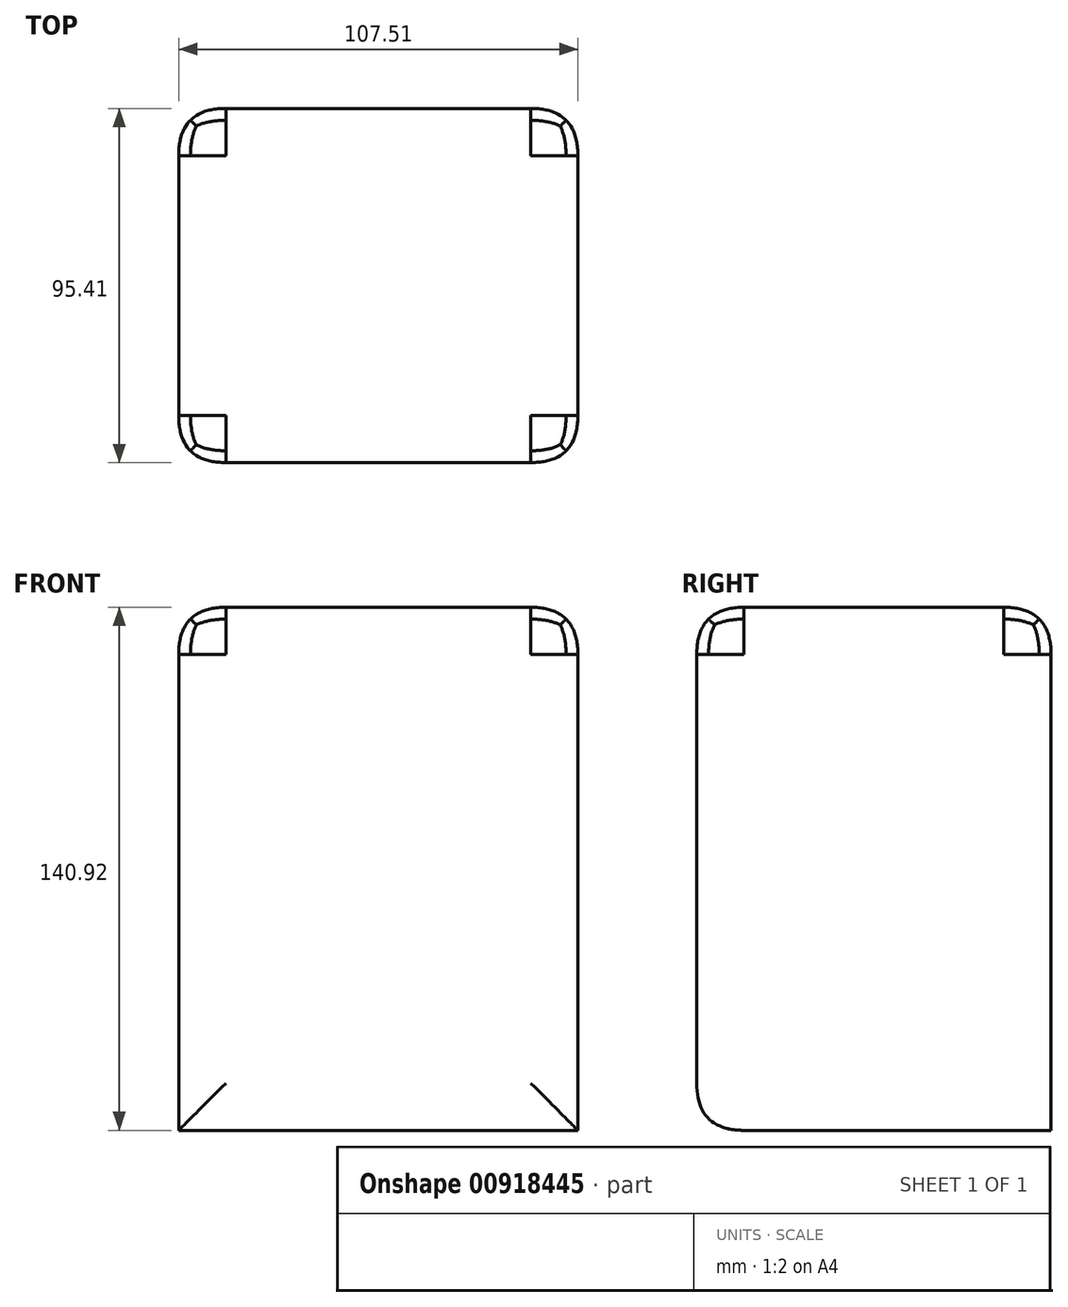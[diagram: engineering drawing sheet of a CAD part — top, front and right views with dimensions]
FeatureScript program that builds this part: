
annotation { "Feature Type Name" : "Feature", "Feature Type Description" : "" }
export const myFeature = defineFeature(function(context is Context, id is Id, definition is map)
    precondition{}
    {
        {
            var Q0;
            Q0=qCreatedBy(makeId("Top.planeOp"),FACE);
            var sketch = newSketch(context, id + "F0", { "sketchPlane" : qUnion([Q0])});
            skLineSegment(sketch, "E0.bottom", {"start": v(-55.9, 40.17) * mm, "end": v(51.6, 40.17) * mm});
            skLineSegment(sketch, "E0.top", {"start": v(-55.9, -55.24) * mm, "end": v(51.6, -55.24) * mm});
            skLineSegment(sketch, "E0.left", {"start": v(-55.9, 40.17) * mm, "end": v(-55.9, -55.24) * mm});
            skLineSegment(sketch, "E0.right", {"start": v(51.6, 40.17) * mm, "end": v(51.6, -55.24) * mm});
            skSolve(sketch);
        }
        {
            var Q0;
            Q0=makeQuery(id+"F0.imprint","IMPRINT",FACE,{"disambiguationData":[TD([[makeQuery(id+"F0.imprint","IMPRINT",EDGE,{"derivedFrom":sQuery(id+"F0.wireOp",EDGE,"E0.bottom")}),-1.0]])]});
            extrude(context, id + "F1", {"entities" : qUnion([Q0]), "depth" : 140.92 * mm, "offsetDistance" : 25.4 * mm});
        }
        {
            var Q0;
            Q0=makeQuery(id+"F1.opExtrude","SWEPT_FACE",FACE,{"disambiguationData":[OSD([sQuery(id+"F0.wireOp",EDGE,"E0.top")])]});
            var Q1;
            Q1=makeQuery(id+"F1.opExtrude","SWEPT_EDGE",EDGE,{"disambiguationData":[OSD([sQuery(id+"F0.wireOp",EDGE,"E0.top"),sQuery(id+"F0.wireOp",EDGE,"E0.left")])]});
            var Q2;
            Q2=makeQuery(id+"F1.opExtrude","SWEPT_EDGE",EDGE,{"disambiguationData":[OSD([sQuery(id+"F0.wireOp",EDGE,"E0.bottom"),sQuery(id+"F0.wireOp",EDGE,"E0.right")])]});
            var Q3;
            Q3=makeQuery(id+"F1.opExtrude","SWEPT_EDGE",EDGE,{"disambiguationData":[OSD([sQuery(id+"F0.wireOp",EDGE,"E0.bottom"),sQuery(id+"F0.wireOp",EDGE,"E0.left")])]});
            var Q4;
            Q4=makeQuery(id+"F1.opExtrude","SWEPT_EDGE",EDGE,{"disambiguationData":[OSD([sQuery(id+"F0.wireOp",EDGE,"E0.top"),sQuery(id+"F0.wireOp",EDGE,"E0.right")])]});
            var Q5;
            Q5=makeQuery(id+"F1.opExtrude","CAP_EDGE",EDGE,{"disambiguationData":[OSD([sQuery(id+"F0.wireOp",EDGE,"E0.top")])],"isStart":false});
            var Q6;
            Q6=makeQuery(id+"F1.opExtrude","CAP_EDGE",EDGE,{"disambiguationData":[OSD([sQuery(id+"F0.wireOp",EDGE,"E0.bottom")])],"isStart":false});
            var Q7;
            Q7=makeQuery(id+"F1.opExtrude","CAP_EDGE",EDGE,{"disambiguationData":[OSD([sQuery(id+"F0.wireOp",EDGE,"E0.right")])],"isStart":false});
            var Q8;
            Q8=makeQuery(id+"F1.opExtrude","CAP_EDGE",EDGE,{"disambiguationData":[OSD([sQuery(id+"F0.wireOp",EDGE,"E0.left")])],"isStart":false});
            fillet(context, id + "F2", {"entities" : qUnion([Q0, Q1, Q2, Q3, Q4, Q5, Q6, Q7, Q8]), "radius" : 12.7 * mm, "tangentPropagation" : true, "rho" : 0.5, "crossSection" : FilletCrossSection.CONIC, "allowEdgeOverflow" : false});
        }
    });
